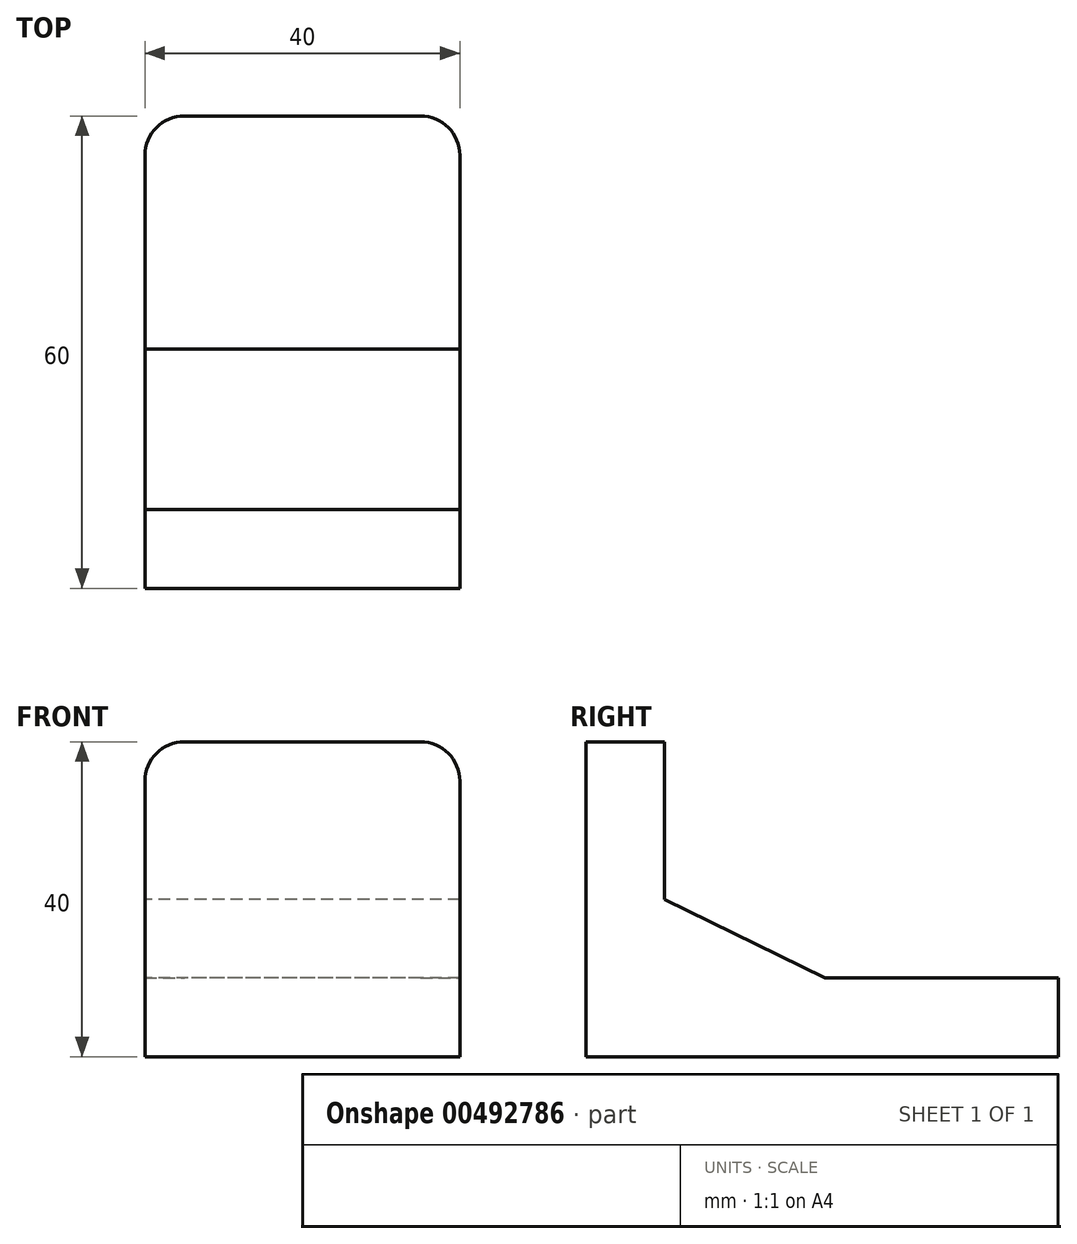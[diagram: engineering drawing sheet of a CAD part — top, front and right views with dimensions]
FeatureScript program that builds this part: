
annotation { "Feature Type Name" : "Feature", "Feature Type Description" : "" }
export const myFeature = defineFeature(function(context is Context, id is Id, definition is map)
    precondition{}
    {
        {
            var Q0;
            Q0=qCreatedBy(makeId("Right.planeOp"),FACE);
            var sketch = newSketch(context, id + "F0", { "sketchPlane" : qUnion([Q0])});
            skLineSegment(sketch, "E0", {"start": v(0, 0) * mm, "end": v(0, 40) * mm});
            skLineSegment(sketch, "E1", {"start": v(0, 40) * mm, "end": v(10, 40) * mm});
            skLineSegment(sketch, "E2", {"start": v(10, 40) * mm, "end": v(10, 20) * mm});
            skLineSegment(sketch, "E3", {"start": v(0, 0) * mm, "end": v(60, 0) * mm});
            skLineSegment(sketch, "E4", {"start": v(60, 0) * mm, "end": v(60, 10) * mm});
            skLineSegment(sketch, "E5", {"start": v(10, 20) * mm, "end": v(30.39, 10) * mm});
            skLineSegment(sketch, "E6", {"start": v(60, 10) * mm, "end": v(30.39, 10) * mm});
            skSolve(sketch);
        }
        {
            var Q0;
            Q0=makeQuery(id+"F0.imprint","IMPRINT",FACE,{"disambiguationData":[TD([[makeQuery(id+"F0.imprint","IMPRINT",EDGE,{"derivedFrom":sQuery(id+"F0.wireOp",EDGE,"E0")}),-1.0]])]});
            extrude(context, id + "F1", {"entities" : qUnion([Q0]), "depth" : 40 * mm});
        }
        {
            var Q0;
            Q0=makeQuery(id+"F1.opExtrude","CAP_EDGE",EDGE,{"disambiguationData":[OSD([sQuery(id+"F0.wireOp",EDGE,"E1")])],"isStart":true});
            var Q1;
            Q1=makeQuery(id+"F1.opExtrude","CAP_EDGE",EDGE,{"disambiguationData":[OSD([sQuery(id+"F0.wireOp",EDGE,"E1")])],"isStart":false});
            var Q2;
            Q2=makeQuery(id+"F1.opExtrude","CAP_EDGE",EDGE,{"disambiguationData":[OSD([sQuery(id+"F0.wireOp",EDGE,"E4")])],"isStart":true});
            var Q3;
            Q3=makeQuery(id+"F1.opExtrude","CAP_EDGE",EDGE,{"disambiguationData":[OSD([sQuery(id+"F0.wireOp",EDGE,"E4")])],"isStart":false});
            fillet(context, id + "F2", {"entities" : qUnion([Q0, Q1, Q2, Q3]), "radius" : 5 * mm, "tangentPropagation" : true, "allowEdgeOverflow" : false});
        }
    });
